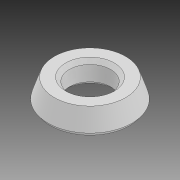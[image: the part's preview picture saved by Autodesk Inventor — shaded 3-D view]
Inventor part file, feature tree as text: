
AUTODESK INVENTOR PART (.ipt)
format: ipt  version: 2020 (Build 240168000, 168)  size: 102,912 bytes
history: native  units: mm
features: revolve x1, chamfer x1, sketch x1
ambient origin geometry x8: Origin, YZ Plane, XZ Plane, XY Plane, X Axis, Y Axis, Z Axis, Center Point
bodies: Solid1 (feature_tree)
feature tree (3):
  revolve  "Revolution1"  [1 undecoded]
  chamfer  "Chamfer1"  Distance=2.0mm
  sketch  "Sketch1"  dims[d0=2.75mm d1=3.0mm d2=2.0mm d3=3.0mm d4=90.0deg d5=0.5mm d6=2.0mm d7=45.0deg]
note: 1 required parameter value undecoded (feature->parameter linkage not recoverable at this tier; creation-order binding heuristic only, values carry confidence <= 0.55)
